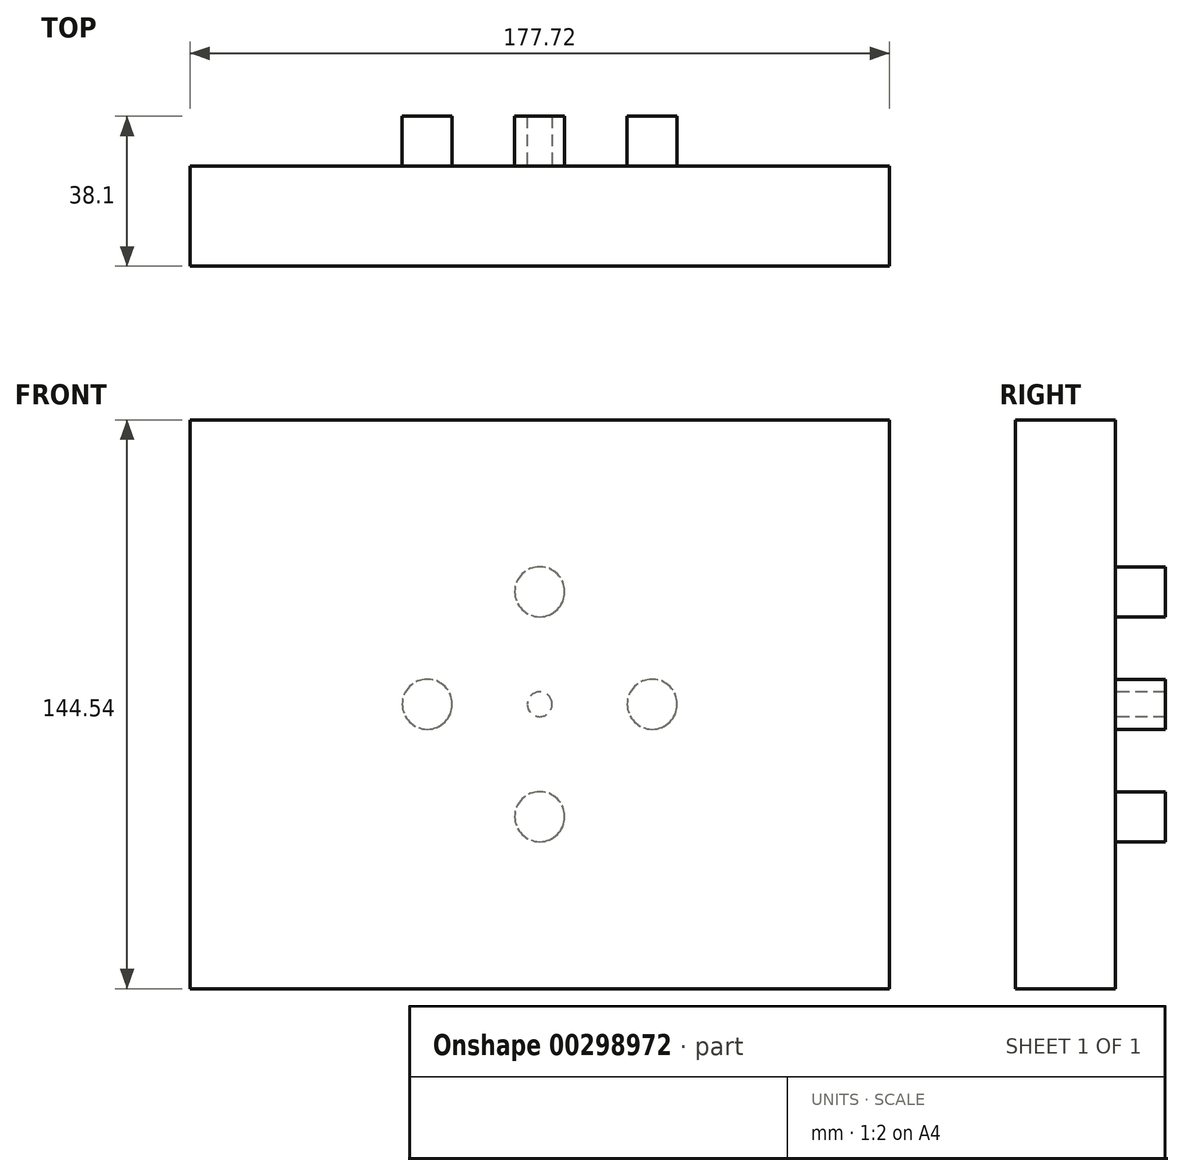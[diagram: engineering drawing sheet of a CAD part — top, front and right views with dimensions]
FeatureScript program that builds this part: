
annotation { "Feature Type Name" : "Feature", "Feature Type Description" : "" }
export const myFeature = defineFeature(function(context is Context, id is Id, definition is map)
    precondition{}
    {
        {
            var Q0;
            Q0=qCreatedBy(makeId("Front.planeOp"),FACE);
            var sketch = newSketch(context, id + "F0", { "sketchPlane" : qUnion([Q0])});
            skLineSegment(sketch, "E0.bottom", {"start": v(-88.86, 72.27) * mm, "end": v(88.86, 72.27) * mm});
            skLineSegment(sketch, "E0.top", {"start": v(-88.86, -72.27) * mm, "end": v(88.86, -72.27) * mm});
            skLineSegment(sketch, "E0.left", {"start": v(-88.86, 72.27) * mm, "end": v(-88.86, -72.27) * mm});
            skLineSegment(sketch, "E0.right", {"start": v(88.86, 72.27) * mm, "end": v(88.86, -72.27) * mm});
            skPoint(sketch, "E0.middle", {"position": v(0, 0) * mm});
            skLineSegment(sketch, "E1", {"start": v(0, 72.27) * mm, "end": v(0, -72.27) * mm, "construction": true});
            skLineSegment(sketch, "E2", {"start": v(-88.86, 0) * mm, "end": v(88.86, 0) * mm, "construction": true});
            skSolve(sketch);
        }
        {
            var Q0;
            Q0 = qSketchRegion(id + "F0", true);
            extrude(context, id + "F1", {"entities" : qUnion([Q0]), "depth" : 25.4 * mm});
        }
        {
            var Q0;
            Q0=makeQuery(id+"F1.opExtrude","CAP_FACE",FACE,{"disambiguationData":[OSD([sQuery(id+"F0.wireOp",EDGE,"E0.bottom"),sQuery(id+"F0.wireOp",EDGE,"E0.top"),sQuery(id+"F0.wireOp",EDGE,"E0.left"),sQuery(id+"F0.wireOp",EDGE,"E0.right")])],"isStart":true});
            var sketch = newSketch(context, id + "F2", { "sketchPlane" : qUnion([Q0])});
            skLineSegment(sketch, "E3", {"start": v(88.86, 0) * mm, "end": v(-88.86, 0) * mm, "construction": true});
            skLineSegment(sketch, "E4", {"start": v(0, 72.27) * mm, "end": v(0, -72.27) * mm, "construction": true});
            skSolve(sketch);
        }
        {
            var Q0;
            Q0=makeQuery(id+"F2.imprint","IMPRINT",FACE,{"disambiguationData":[TD([[makeQuery(id+"F2.imprint","IMPRINT",EDGE,{"derivedFrom":makeQuery(id+"F1.opExtrude","CAP_EDGE",EDGE,{"disambiguationData":[OSD([sQuery(id+"F0.wireOp",EDGE,"E0.bottom")])],"isStart":true})}),1.0]])]});
            var sketch = newSketch(context, id + "F3", { "sketchPlane" : qUnion([Q0])});
            skCircle(sketch, "E5", {"center": v(0, 0) * mm, "radius": 3.18 * mm});
            skSolve(sketch);
        }
        {
            var Q0;
            Q0 = qSketchRegion(id + "F3", true);
            extrude(context, id + "F4", {"entities" : qUnion([Q0]), "operationType" : NewBodyOperationType.ADD, "depth" : 12.7 * mm});
        }
        {
            var Q0;
            Q0=makeQuery(id+"F2.imprint","IMPRINT",FACE,{"disambiguationData":[TD([[makeQuery(id+"F2.imprint","IMPRINT",EDGE,{"derivedFrom":makeQuery(id+"F1.opExtrude","CAP_EDGE",EDGE,{"disambiguationData":[OSD([sQuery(id+"F0.wireOp",EDGE,"E0.bottom")])],"isStart":true})}),1.0]])]});
            var sketch = newSketch(context, id + "F5", { "sketchPlane" : qUnion([Q0])});
            skLineSegment(sketch, "E6", {"start": v(0, 0) * mm, "end": v(28.58, 0) * mm, "construction": true});
            skCircle(sketch, "E7", {"center": v(28.58, 0) * mm, "radius": 6.35 * mm, "construction": true});
            skLineSegment(sketch, "E8", {"start": v(0, 0) * mm, "end": v(0, 28.58) * mm, "construction": true});
            skLineSegment(sketch, "E9", {"start": v(0, 28.58) * mm, "end": v(0, 0) * mm, "construction": true});
            skLineSegment(sketch, "E10", {"start": v(-28.58, 0) * mm, "end": v(0, 0) * mm, "construction": true});
            skLineSegment(sketch, "E11", {"start": v(0, 0) * mm, "end": v(0, -28.58) * mm, "construction": true});
            skCircle(sketch, "E12", {"center": v(0, 28.58) * mm, "radius": 6.35 * mm, "construction": true});
            skCircle(sketch, "E13", {"center": v(-28.58, 0) * mm, "radius": 6.35 * mm, "construction": true});
            skCircle(sketch, "E14", {"center": v(0, -28.58) * mm, "radius": 6.35 * mm, "construction": true});
            skCircle(sketch, "E15", {"center": v(0, 28.58) * mm, "radius": 6.35 * mm});
            skCircle(sketch, "E16", {"center": v(-28.58, 0) * mm, "radius": 6.35 * mm});
            skCircle(sketch, "E17", {"center": v(0, -28.58) * mm, "radius": 6.35 * mm});
            skCircle(sketch, "E18", {"center": v(28.58, 0) * mm, "radius": 6.35 * mm});
            skSolve(sketch);
        }
        {
            var Q0;
            Q0=makeQuery(id+"F5.imprint","IMPRINT",FACE,{"disambiguationData":[TD([[makeQuery(id+"F5.imprint","IMPRINT",EDGE,{"derivedFrom":sQuery(id+"F5.wireOp",EDGE,"E16")}),1.0]])]});
            var Q1;
            Q1=makeQuery(id+"F5.imprint","IMPRINT",FACE,{"disambiguationData":[TD([[makeQuery(id+"F5.imprint","IMPRINT",EDGE,{"derivedFrom":sQuery(id+"F5.wireOp",EDGE,"E15")}),1.0]])]});
            var Q2;
            Q2=makeQuery(id+"F5.imprint","IMPRINT",FACE,{"disambiguationData":[TD([[makeQuery(id+"F5.imprint","IMPRINT",EDGE,{"derivedFrom":sQuery(id+"F5.wireOp",EDGE,"E18")}),1.0]])]});
            var Q3;
            Q3=makeQuery(id+"F5.imprint","IMPRINT",FACE,{"disambiguationData":[TD([[makeQuery(id+"F5.imprint","IMPRINT",EDGE,{"derivedFrom":sQuery(id+"F5.wireOp",EDGE,"E17")}),1.0]])]});
            extrude(context, id + "F6", {"entities" : qUnion([Q0, Q1, Q2, Q3]), "operationType" : NewBodyOperationType.ADD, "depth" : 12.7 * mm});
        }
    });
